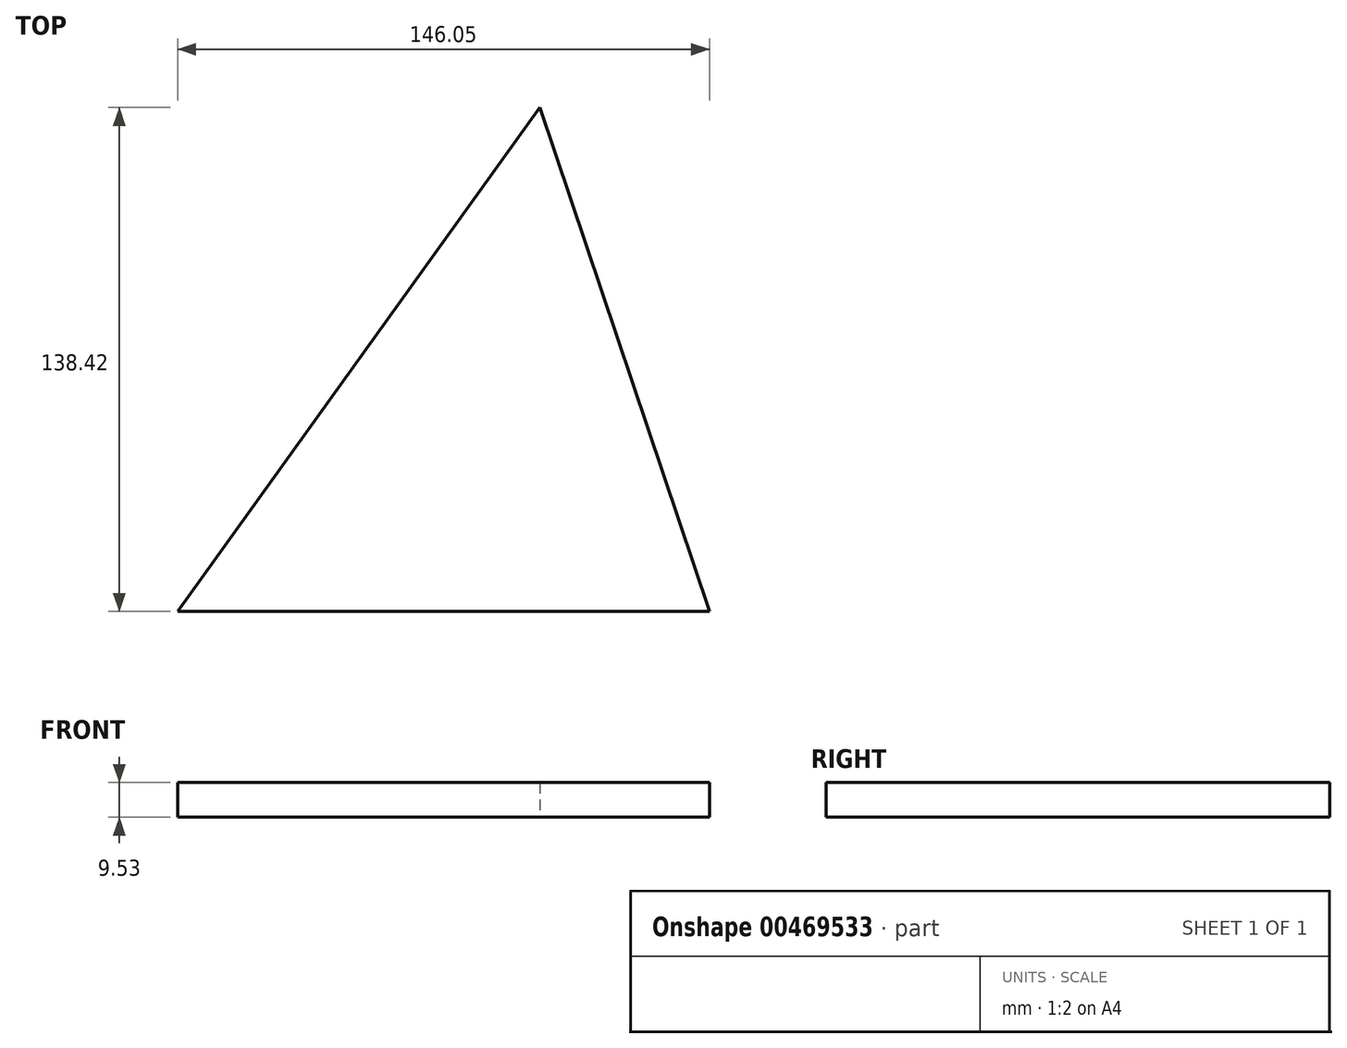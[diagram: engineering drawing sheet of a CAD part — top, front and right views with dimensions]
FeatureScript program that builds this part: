
annotation { "Feature Type Name" : "Feature", "Feature Type Description" : "" }
export const myFeature = defineFeature(function(context is Context, id is Id, definition is map)
    precondition{}
    {
        {
            var Q0;
            Q0=qCreatedBy(makeId("Top.planeOp"),FACE);
            var sketch = newSketch(context, id + "F0", { "sketchPlane" : qUnion([Q0])});
            skLineSegment(sketch, "E0", {"start": v(0, 0) * mm, "end": v(99.47, 138.42) * mm});
            skLineSegment(sketch, "E1", {"start": v(99.47, 138.42) * mm, "end": v(146.05, 0) * mm});
            skLineSegment(sketch, "E2", {"start": v(146.05, 0) * mm, "end": v(0, 0) * mm});
            skSolve(sketch);
        }
        {
            var Q0;
            Q0 = qSketchRegion(id + "F0", true);
            extrude(context, id + "F1", {"entities" : qUnion([Q0]), "depth" : 9.52 * mm, "offsetDistance" : 25.4 * mm});
        }
    });
